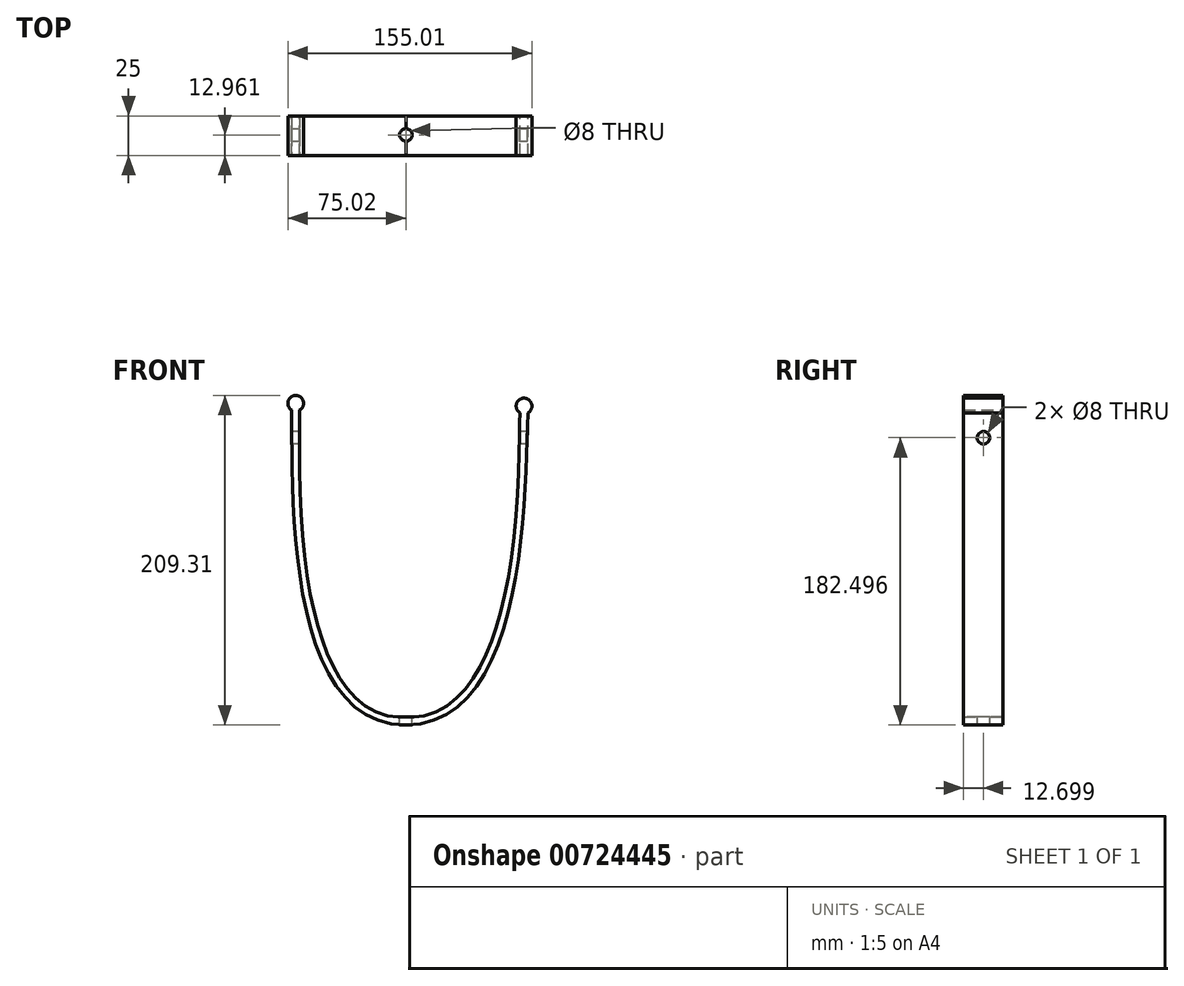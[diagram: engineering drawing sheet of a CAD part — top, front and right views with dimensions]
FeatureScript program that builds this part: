
annotation { "Feature Type Name" : "Feature", "Feature Type Description" : "" }
export const myFeature = defineFeature(function(context is Context, id is Id, definition is map)
    precondition{}
    {
        {
            var Q0;
            Q0=qCreatedBy(makeId("Front.planeOp"),FACE);
            var sketch = newSketch(context, id + "F0", { "sketchPlane" : qUnion([Q0])});
            skFitSpline(sketch, "E0", {"points": [v(-72.52, 136.67) * mm, v(0, -63.33) * mm], "startDerivative": vector(0, -178.07) * mm, "endDerivative": vector(225.44, 0.05) * mm});
            skFitSpline(sketch, "E1.MirrorCS", {"points": [v(77.39, 134.86) * mm, v(0, -63.33) * mm], "startDerivative": vector(-4.29, -178.02) * mm, "endDerivative": vector(-224.81, -0.45) * mm});
            skFitSpline(sketch, "E2.0", {"points": [v(-67.52, 136.67) * mm, v(-67.52, 129.23) * mm, v(-67.6, 111.9) * mm, v(-67.03, 80.97) * mm, v(-64.84, 47.76) * mm, v(-60.9, 20.38) * mm, v(-56.04, 0) * mm, v(-51.46, -14.18) * mm, v(-45.86, -26.9) * mm, v(-39.18, -37.83) * mm, v(-31.4, -46.67) * mm, v(-22.48, -53.2) * mm, v(-12.25, -57.33) * mm, v(-4.3, -58.33) * mm, v(0, -58.33) * mm]});
            skFitSpline(sketch, "E2.1", {"points": [v(72.39, 134.99) * mm, v(72.2, 127.55) * mm, v(71.86, 110.28) * mm, v(70.52, 79.6) * mm, v(67.5, 46.7) * mm, v(62.87, 19.62) * mm, v(57.5, -0.53) * mm, v(52.57, -14.55) * mm, v(46.66, -27.13) * mm, v(39.7, -37.95) * mm, v(31.7, -46.71) * mm, v(22.6, -53.21) * mm, v(12.25, -57.31) * mm, v(4.29, -58.32) * mm, v(-0.01, -58.33) * mm]});
            skCircle(sketch, "E3", {"center": v(-70.02, 140.98) * mm, "radius": 5 * mm});
            skCircle(sketch, "E4", {"center": v(75, 139.24) * mm, "radius": 5 * mm});
            skSolve(sketch);
        }
        {
            var Q0;
            {var subQ7=sQuery(id+"F0.wireOp",EDGE,"E1.MirrorCS");var subQ8=sQuery(id+"F0.wireOp",EDGE,"E0");var subQ9=makeQuery(id+"F0.imprint","INTERSECT",VERTEX,{"derivedFrom":[subQ8,subQ7]});Q0=makeQuery(id+"F0.imprint","IMPRINT",FACE,{"disambiguationData":[TD([[makeQuery(id+"F0.imprint","IMPRINT",EDGE,{"disambiguationData":[TD([[subQ9,1.0]])],"derivedFrom":subQ8}),1.0]])]});}
            var Q1;
            {var subQ0=sQuery(id+"F0.wireOp",EDGE,"E4");var subQ1=makeQuery(id+"F0.imprint","INTERSECT",VERTEX,{"derivedFrom":[sQuery(id+"F0.wireOp",EDGE,"E1.MirrorCS"),subQ0]});Q1=makeQuery(id+"F0.imprint","IMPRINT",FACE,{"disambiguationData":[TD([[makeQuery(id+"F0.imprint","IMPRINT",EDGE,{"disambiguationData":[TD([[subQ1,1.0]])],"derivedFrom":subQ0}),1.0]])]});}
            var Q2;
            {var subQ0=sQuery(id+"F0.wireOp",EDGE,"E3");var subQ1=makeQuery(id+"F0.imprint","INTERSECT",VERTEX,{"derivedFrom":[sQuery(id+"F0.wireOp",EDGE,"E0"),subQ0]});Q2=makeQuery(id+"F0.imprint","IMPRINT",FACE,{"disambiguationData":[TD([[makeQuery(id+"F0.imprint","IMPRINT",EDGE,{"disambiguationData":[TD([[subQ1,-1.0]])],"derivedFrom":subQ0}),1.0]])]});}
            extrude(context, id + "F1", {"entities" : qUnion([Q0, Q1, Q2]), "depth" : 25 * mm, "offsetDistance" : 25 * mm});
        }
        {
            var Q0;
            Q0=qCreatedBy(makeId("Right.planeOp"),FACE);
            var sketch = newSketch(context, id + "F2", { "sketchPlane" : qUnion([Q0])});
            skCircle(sketch, "E5", {"center": v(-12.3, 119.17) * mm, "radius": 4 * mm});
            skSolve(sketch);
        }
        {
            var Q0;
            Q0=makeQuery(id+"F2.imprint","IMPRINT",FACE,{"disambiguationData":[TD([[makeQuery(id+"F2.imprint","IMPRINT",EDGE,{"derivedFrom":sQuery(id+"F2.wireOp",EDGE,"E5")}),1.0]])]});
            extrude(context, id + "F3", {"entities" : qUnion([Q0]), "operationType" : NewBodyOperationType.REMOVE, "endBound" : BoundingType.SYMMETRIC, "depth" : 200 * mm, "offsetDistance" : 25 * mm});
        }
        {
            var Q0;
            Q0=qCreatedBy(makeId("Top.planeOp"),FACE);
            var sketch = newSketch(context, id + "F4", { "sketchPlane" : qUnion([Q0])});
            skCircle(sketch, "E6", {"center": v(0, -12.04) * mm, "radius": 4 * mm});
            skSolve(sketch);
        }
        {
            var Q0;
            Q0=makeQuery(id+"F4.imprint","IMPRINT",FACE,{"disambiguationData":[TD([[makeQuery(id+"F4.imprint","IMPRINT",EDGE,{"derivedFrom":sQuery(id+"F4.wireOp",EDGE,"E6")}),1.0]])]});
            extrude(context, id + "F5", {"entities" : qUnion([Q0]), "operationType" : NewBodyOperationType.REMOVE, "oppositeDirection" : true, "depth" : 200 * mm, "offsetDistance" : 25 * mm});
        }
    });
